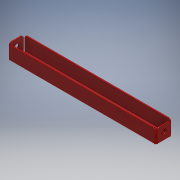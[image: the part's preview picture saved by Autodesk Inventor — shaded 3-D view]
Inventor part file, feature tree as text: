
AUTODESK INVENTOR PART (.ipt)
format: ipt  version: 2018 (Build 220112000, 112)  size: 172,032 bytes
history: native  units: mm
features: other x7, sketch x4, hole x2
ambient origin geometry x8: Origin, YZ Plane, XZ Plane, XY Plane, X Axis, Y Axis, Z Axis, Center Point
bodies: Solido1 (feature_tree)
feature tree (13):
  other  "Faccia1"
  other  "Flangia1"
  hole  "Foro1"  [1 undecoded]
  hole  "Foro2"  [1 undecoded]
  other  "Arrotondamento angolo1"
  sketch  "Schizzo1"
  other  "Piano1"
  sketch  "Schizzo2"
  other  "Piano2"
  other  "Piega (Bend)1"
  other  "Angolo1"
  sketch  "Schizzo3"
  sketch  "Schizzo4"
note: 2 required parameter values undecoded (feature->parameter linkage not recoverable at this tier; creation-order binding heuristic only, values carry confidence <= 0.55)
